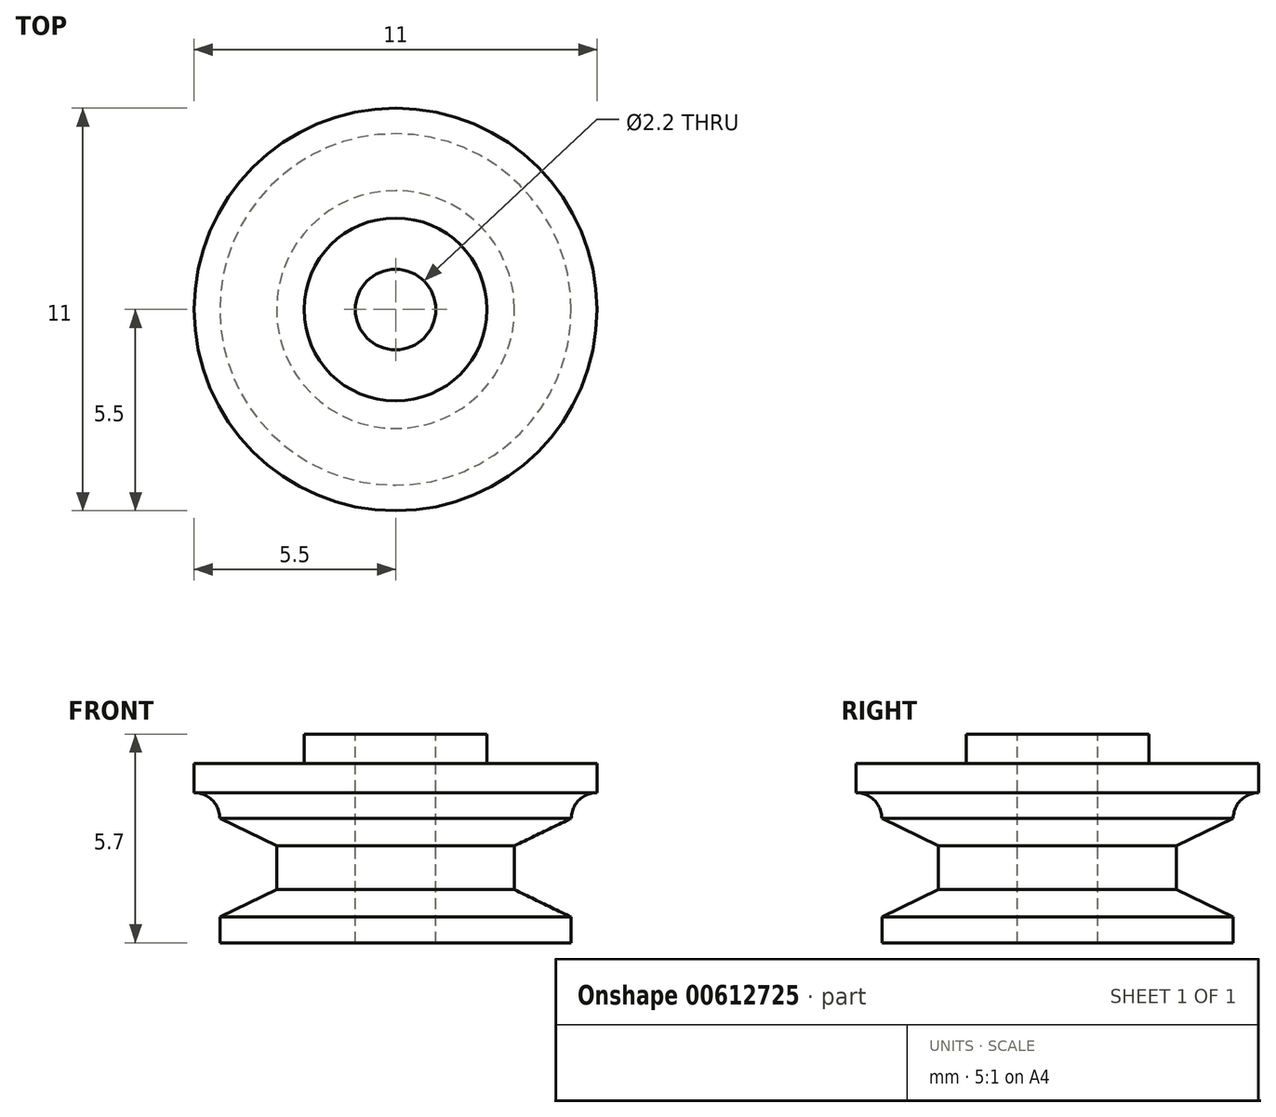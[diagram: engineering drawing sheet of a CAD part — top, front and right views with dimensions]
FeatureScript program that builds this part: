
annotation { "Feature Type Name" : "Feature", "Feature Type Description" : "" }
export const myFeature = defineFeature(function(context is Context, id is Id, definition is map)
    precondition{}
    {
        {
            var Q0;
            Q0=qCreatedBy(makeId("Front.planeOp"),FACE);
            var sketch = newSketch(context, id + "F0", { "sketchPlane" : qUnion([Q0])});
            skLineSegment(sketch, "E0", {"start": v(0, 0) * mm, "end": v(-4.8, 0) * mm});
            skLineSegment(sketch, "E1", {"start": v(-4.8, 0) * mm, "end": v(-4.8, 0.7) * mm});
            skLineSegment(sketch, "E2", {"start": v(-4.8, 0.7) * mm, "end": v(-3.25, 1.45) * mm});
            skLineSegment(sketch, "E3", {"start": v(-3.25, 1.45) * mm, "end": v(-3.25, 2.65) * mm});
            skLineSegment(sketch, "E4", {"start": v(-3.25, 2.65) * mm, "end": v(-4.8, 3.4) * mm});
            skLineSegment(sketch, "E5", {"start": v(-4.8, 3.4) * mm, "end": v(-4.8, 4.1) * mm});
            skLineSegment(sketch, "E6", {"start": v(-4.8, 4.1) * mm, "end": v(-5.5, 4.1) * mm});
            skLineSegment(sketch, "E7", {"start": v(-5.5, 4.1) * mm, "end": v(-5.5, 4.9) * mm});
            skLineSegment(sketch, "E8", {"start": v(-5.5, 4.9) * mm, "end": v(-2.5, 4.9) * mm});
            skLineSegment(sketch, "E9", {"start": v(-2.5, 4.9) * mm, "end": v(-2.5, 5.7) * mm});
            skLineSegment(sketch, "E10", {"start": v(-2.5, 5.7) * mm, "end": v(0, 5.7) * mm});
            skLineSegment(sketch, "E11", {"start": v(0, 5.7) * mm, "end": v(0, 0) * mm});
            skLineSegment(sketch, "E12", {"start": v(-9.92, 2.05) * mm, "end": v(5.15, 2.05) * mm, "construction": true});
            skSolve(sketch);
        }
        {
            var Q0;
            Q0=qSketchRegion(id+"F0",true);
            var Q1;
            Q1=sQuery(id+"F0.wireOp",EDGE,"E11");
            revolve(context, id + "F1", {"entities" : qUnion([Q0]), "axis" : qUnion([Q1]), "revolveType" : RevolveType.FULL});
        }
        {
            var Q0;
            Q0=makeQuery(id+"F1.opRevolve","SWEPT_EDGE",EDGE,{"disambiguationData":[OSD([sQuery(id+"F0.wireOp",EDGE,"E5"),sQuery(id+"F0.wireOp",EDGE,"E6")])]});
            fillet(context, id + "F2", {"entities" : qUnion([Q0]), "radius" : 0.7 * mm, "tangentPropagation" : true, "allowEdgeOverflow" : false});
        }
        {
            var Q0;
            Q0=makeQuery(id+"F1.opRevolve","SWEPT_FACE",FACE,{"disambiguationData":[OSD([sQuery(id+"F0.wireOp",EDGE,"E10")])]});
            var sketch = newSketch(context, id + "F3", { "sketchPlane" : qUnion([Q0])});
            skCircle(sketch, "E13", {"center": v(0, 0) * mm, "radius": 1.1 * mm});
            skSolve(sketch);
        }
        {
            var Q0;
            Q0=qSketchRegion(id+"F3",true);
            extrude(context, id + "F4", {"entities" : qUnion([Q0]), "operationType" : NewBodyOperationType.REMOVE, "endBound" : BoundingType.THROUGH_ALL, "oppositeDirection" : true, "depth" : 0.8 * mm, "offsetDistance" : 25 * mm});
        }
    });
